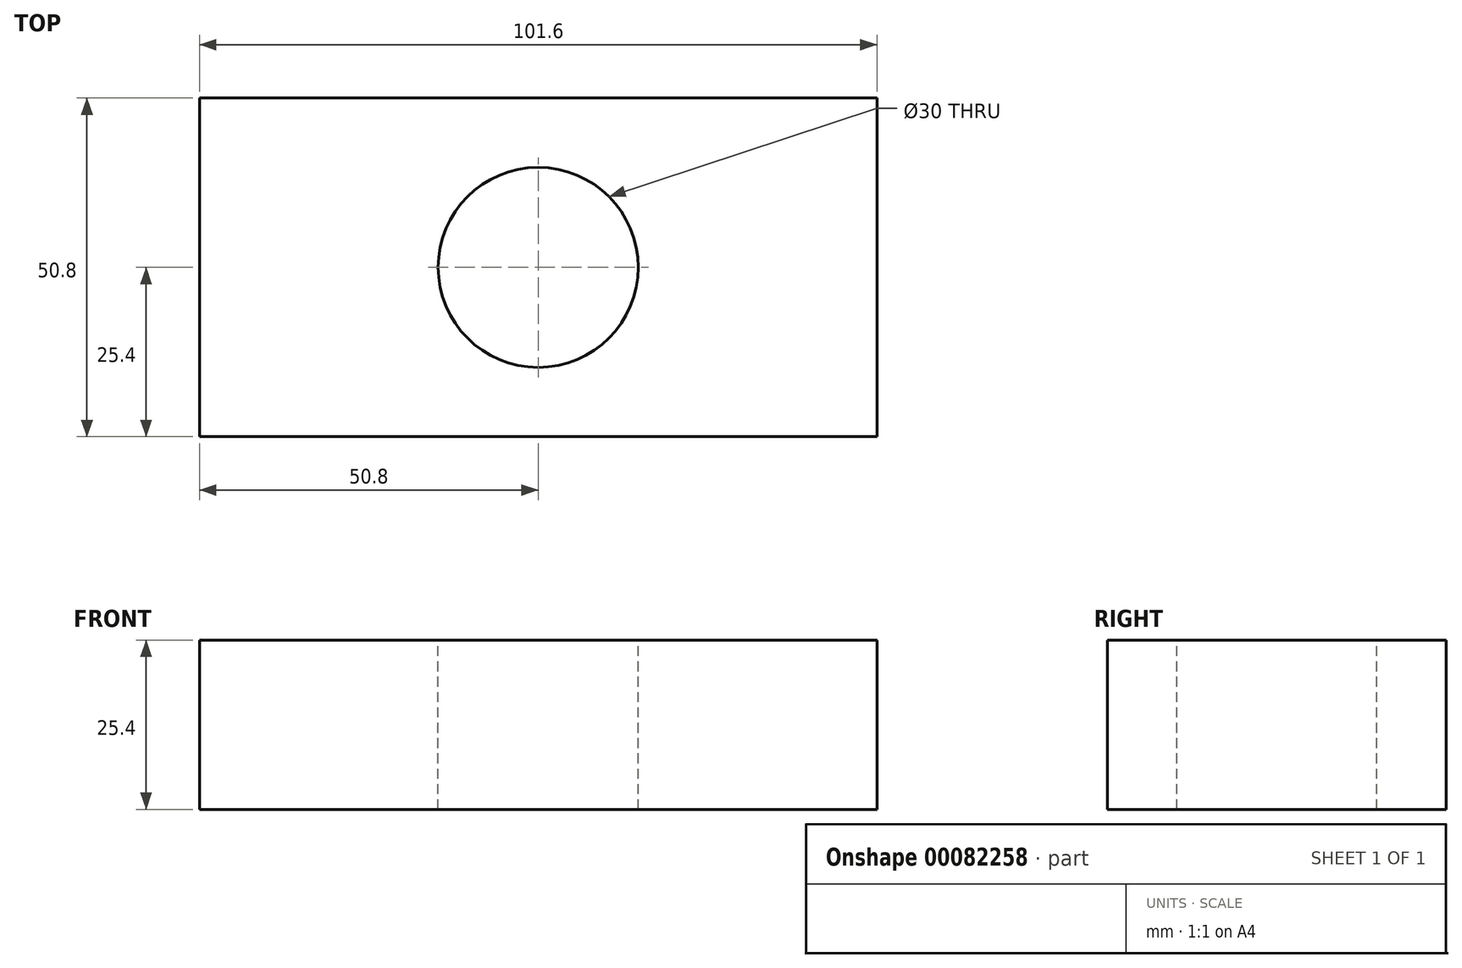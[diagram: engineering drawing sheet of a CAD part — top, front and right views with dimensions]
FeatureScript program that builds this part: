
annotation { "Feature Type Name" : "Feature", "Feature Type Description" : "" }
export const myFeature = defineFeature(function(context is Context, id is Id, definition is map)
    precondition{}
    {
        {
            var Q0;
            Q0=qCreatedBy(makeId("Top.planeOp"),FACE);
            var sketch = newSketch(context, id + "F0", { "sketchPlane" : qUnion([Q0])});
            skLineSegment(sketch, "E0.bottom", {"start": v(50.8, 25.4) * mm, "end": v(-50.8, 25.4) * mm});
            skLineSegment(sketch, "E0.top", {"start": v(50.8, -25.4) * mm, "end": v(-50.8, -25.4) * mm});
            skLineSegment(sketch, "E0.left", {"start": v(50.8, 25.4) * mm, "end": v(50.8, -25.4) * mm});
            skLineSegment(sketch, "E0.right", {"start": v(-50.8, 25.4) * mm, "end": v(-50.8, -25.4) * mm});
            skPoint(sketch, "E0.middle", {"position": v(0, 0) * mm});
            skSolve(sketch);
        }
        {
            var Q0;
            Q0=makeQuery(id+"F0.imprint","IMPRINT",FACE,{"disambiguationData":[TD([[makeQuery(id+"F0.imprint","IMPRINT",EDGE,{"derivedFrom":sQuery(id+"F0.wireOp",EDGE,"E0.bottom")}),1.0]])]});
            extrude(context, id + "F1", {"entities" : qUnion([Q0]), "depth" : 25.4 * mm});
        }
        {
            var Q0;
            Q0=makeQuery(id+"F1.opExtrude","CAP_FACE",FACE,{"disambiguationData":[OSD([sQuery(id+"F0.wireOp",EDGE,"E0.bottom"),sQuery(id+"F0.wireOp",EDGE,"E0.top"),sQuery(id+"F0.wireOp",EDGE,"E0.left"),sQuery(id+"F0.wireOp",EDGE,"E0.right")])],"isStart":false});
            var sketch = newSketch(context, id + "F2", { "sketchPlane" : qUnion([Q0])});
            skCircle(sketch, "E1", {"center": v(0, 0) * mm, "radius": 15 * mm});
            skSolve(sketch);
        }
        {
            var Q0;
            Q0 = qSketchRegion(id + "F2", true);
            extrude(context, id + "F3", {"entities" : qUnion([Q0]), "operationType" : NewBodyOperationType.REMOVE, "endBound" : BoundingType.UP_TO_NEXT, "oppositeDirection" : true, "depth" : 25.4 * mm});
        }
    });
